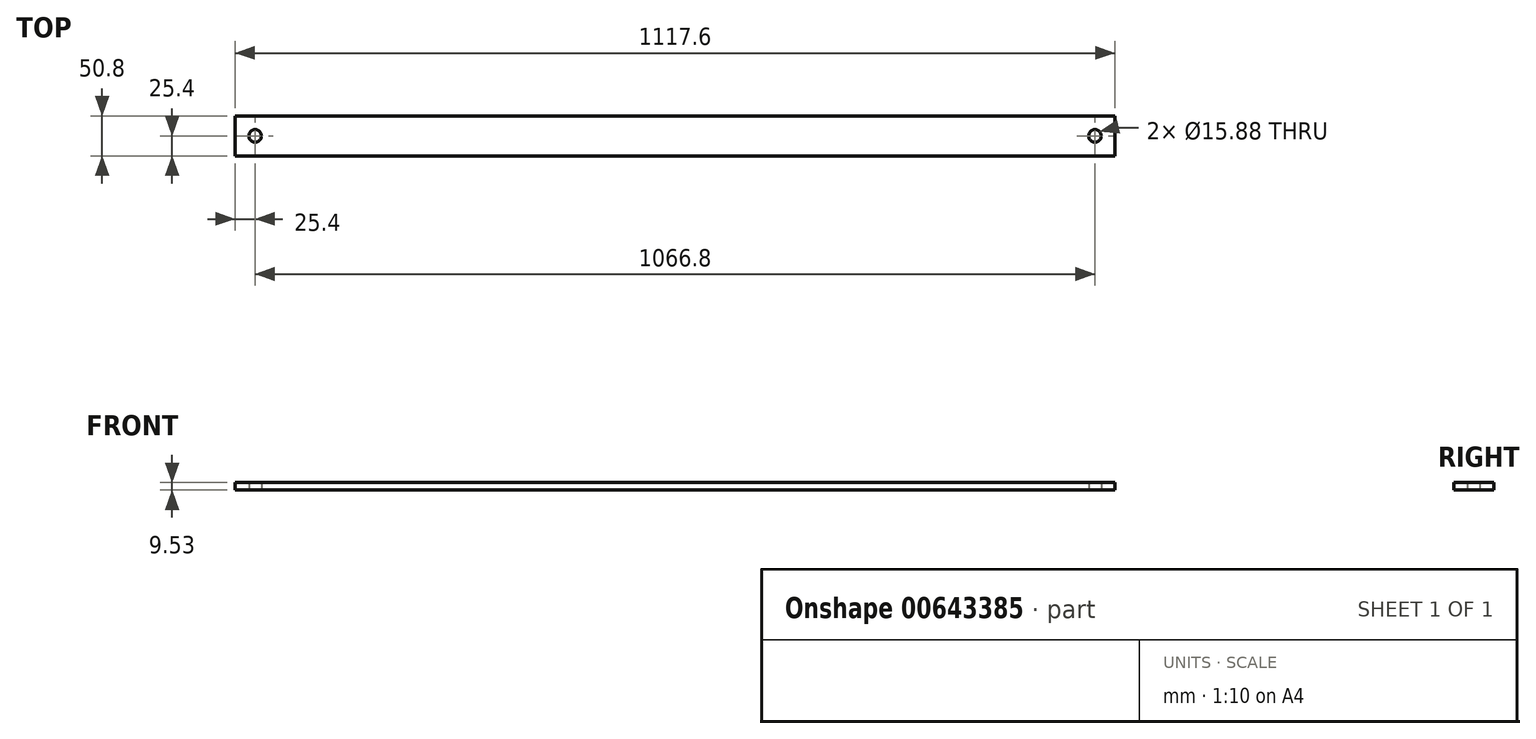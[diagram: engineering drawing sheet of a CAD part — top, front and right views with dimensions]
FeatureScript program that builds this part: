
annotation { "Feature Type Name" : "Feature", "Feature Type Description" : "" }
export const myFeature = defineFeature(function(context is Context, id is Id, definition is map)
    precondition{}
    {
        {
            var Q0;
            Q0=qCreatedBy(makeId("Top.planeOp"),FACE);
            var sketch = newSketch(context, id + "F0", { "sketchPlane" : qUnion([Q0])});
            skLineSegment(sketch, "E0.bottom", {"start": v(558.8, -25.4) * mm, "end": v(-558.8, -25.4) * mm});
            skLineSegment(sketch, "E0.top", {"start": v(558.8, 25.4) * mm, "end": v(-558.8, 25.4) * mm});
            skLineSegment(sketch, "E0.left", {"start": v(558.8, -25.4) * mm, "end": v(558.8, 25.4) * mm});
            skLineSegment(sketch, "E0.right", {"start": v(-558.8, -25.4) * mm, "end": v(-558.8, 25.4) * mm});
            skPoint(sketch, "E0.middle", {"position": v(0, 0) * mm});
            skCircle(sketch, "E1", {"center": v(-533.4, 0) * mm, "radius": 7.94 * mm});
            skPoint(sketch, "E1.centerSnap0", {"position": v(-558.8, 0) * mm});
            skCircle(sketch, "E2.MirrorC", {"center": v(533.4, 0) * mm, "radius": 7.94 * mm});
            skSolve(sketch);
        }
        {
            var Q0;
            Q0 = qSketchRegion(id + "F0", true);
            extrude(context, id + "F1", {"entities" : qUnion([Q0]), "depth" : 9.52 * mm, "offsetDistance" : 25.4 * mm});
        }
    });
